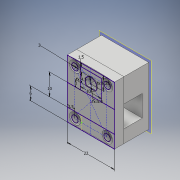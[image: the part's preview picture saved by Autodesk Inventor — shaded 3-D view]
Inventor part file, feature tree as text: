
AUTODESK INVENTOR PART (.ipt)
format: ipt  version: 2017 (Build 210142000, 142)  size: 220,672 bytes
history: native  units: mm
features: extrude x6, sketch x4, plane x1, projected_geometry x1
ambient origin geometry x8: Origin, YZ Plane, XZ Plane, XY Plane, X Axis, Y Axis, Z Axis, Center Point
bodies: Solid1 (feature_tree), Solid2 (feature_tree)
feature tree (12):
  extrude  "Extrusion1"  Depth=4.5mm
  extrude  "Extrusion4"  Depth=6.25mm
  plane  "Work Plane1"
  extrude  "Extrusion5"  Depth=10.0mm
  extrude  "Extrusion6"  Depth=10.0mm
  extrude  "Extrusion7"  Depth=10.0mm
  extrude  "Extrusion8"  Depth=3.5mm
  sketch  "Sketch2"  dims[d1=5.5mm d2=4.5mm]
  sketch  "Sketch3"  dims[d3=4.45mm d4=0.0mm d5=6.25mm]
  sketch  "Sketch4"  dims[d6=22.0mm d8=10.0mm]
  sketch  "Sketch5"  dims[d9=3.0mm d10=6.0mm d11=3.0mm d12=3.5mm d16=10.0mm d17=1.5mm d20=150.0mm d21=9.5mm d22=0.0mm d23=11.5mm d24=9.5mm d25=0.0mm d26=3.0mm d27=0.0mm d28=7.0mm d29=3.0mm d30=0.0mm d31=5.0mm d32=3.0mm d33=0.0mm]
  projected_geometry  "Project Cut Edges1"
